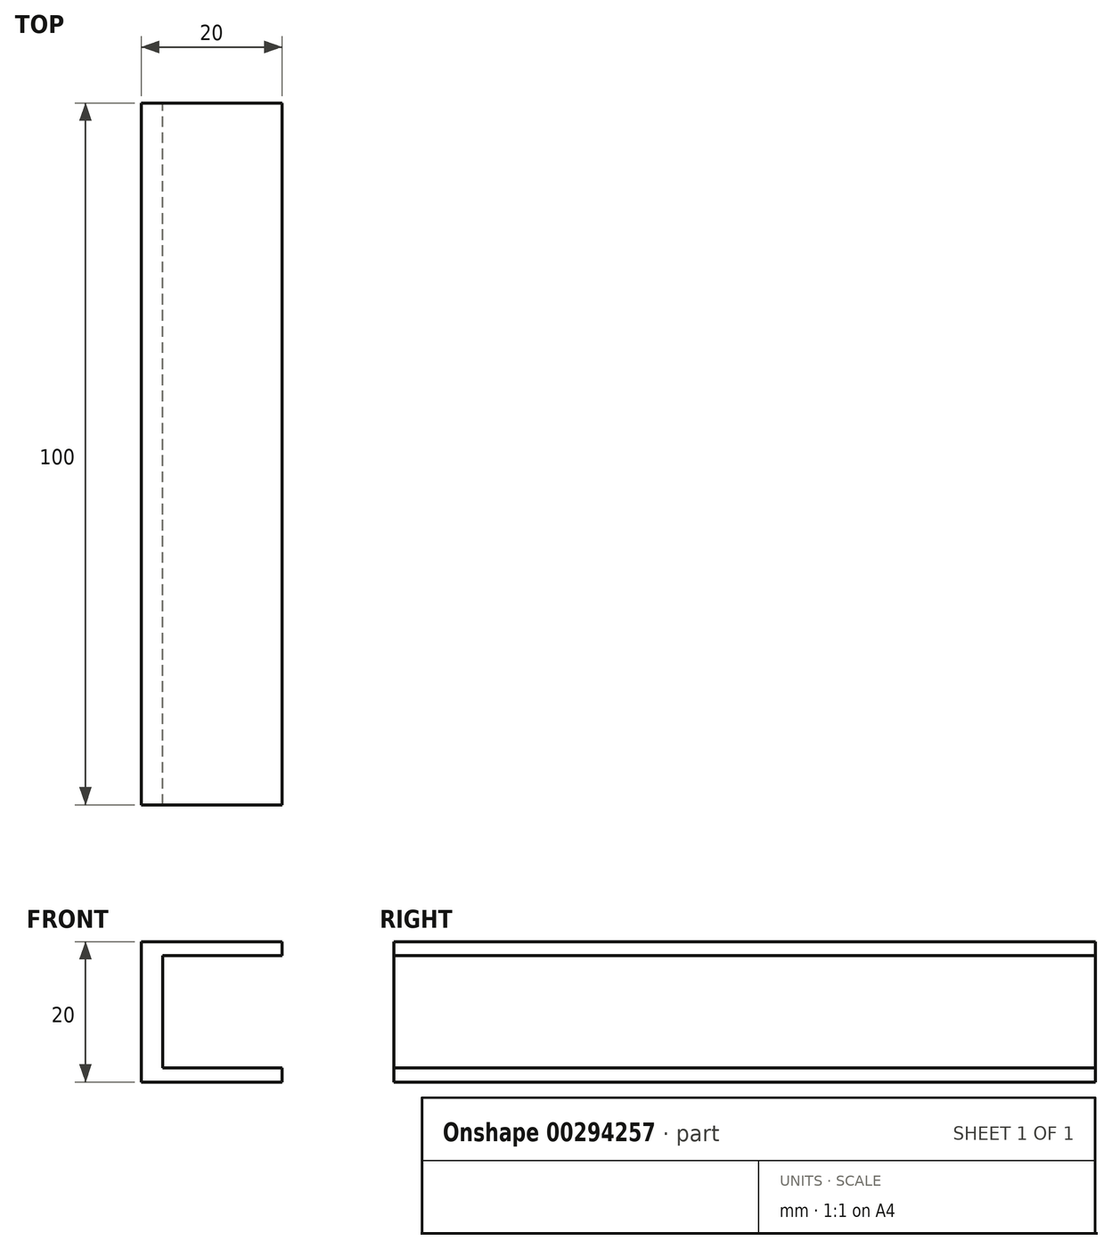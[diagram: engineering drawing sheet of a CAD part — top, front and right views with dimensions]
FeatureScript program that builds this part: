
annotation { "Feature Type Name" : "Feature", "Feature Type Description" : "" }
export const myFeature = defineFeature(function(context is Context, id is Id, definition is map)
    precondition{}
    {
        {
            var Q0;
            Q0=qCreatedBy(makeId("Front.planeOp"),FACE);
            var sketch = newSketch(context, id + "F0", { "sketchPlane" : qUnion([Q0])});
            skLineSegment(sketch, "E0", {"start": v(-20, 18) * mm, "end": v(-20, -2) * mm});
            skLineSegment(sketch, "E1", {"start": v(-20, 18) * mm, "end": v(0, 18) * mm});
            skLineSegment(sketch, "E2", {"start": v(-20, -2) * mm, "end": v(0, -2) * mm});
            skLineSegment(sketch, "E3", {"start": v(0, -2) * mm, "end": v(0, 0) * mm});
            skLineSegment(sketch, "E4", {"start": v(0, 0) * mm, "end": v(-17, 0) * mm});
            skLineSegment(sketch, "E5", {"start": v(-17, 0) * mm, "end": v(-17, 16) * mm});
            skLineSegment(sketch, "E6", {"start": v(-17, 16) * mm, "end": v(0, 16) * mm});
            skLineSegment(sketch, "E7", {"start": v(0, 18) * mm, "end": v(0, 16) * mm});
            skSolve(sketch);
        }
        {
            var Q0;
            Q0 = qSketchRegion(id + "F0", true);
            extrude(context, id + "F1", {"entities" : qUnion([Q0]), "depth" : 100 * mm});
        }
    });
